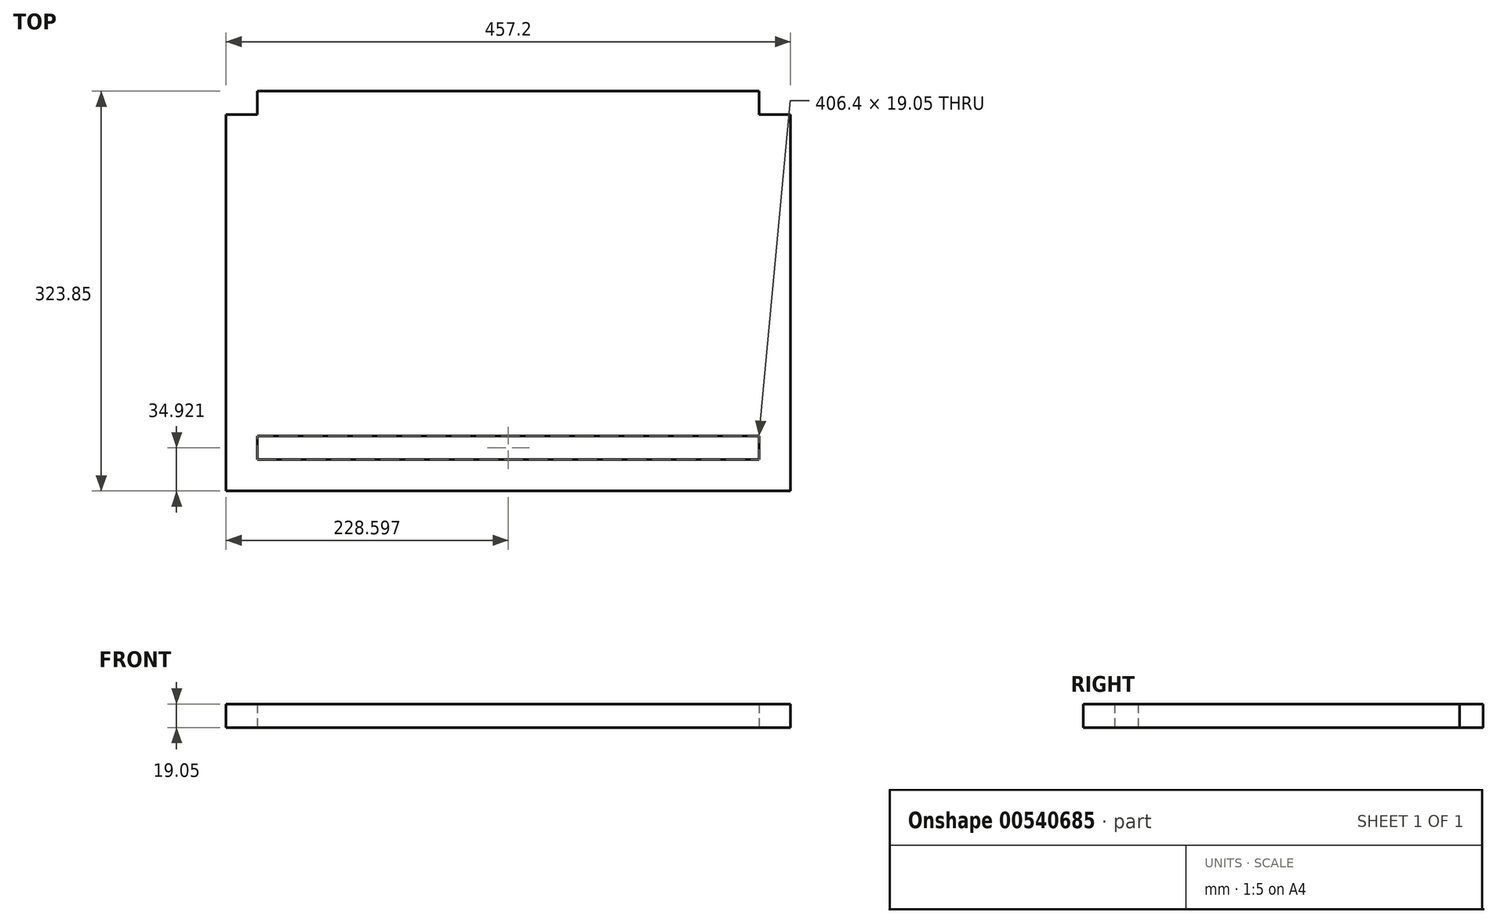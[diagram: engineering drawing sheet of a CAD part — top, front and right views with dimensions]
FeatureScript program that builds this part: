
annotation { "Feature Type Name" : "Feature", "Feature Type Description" : "" }
export const myFeature = defineFeature(function(context is Context, id is Id, definition is map)
    precondition{}
    {
        {
            var Q0;
            Q0=qCreatedBy(makeId("Top.planeOp"),FACE);
            var sketch = newSketch(context, id + "F0", { "sketchPlane" : qUnion([Q0])});
            skLineSegment(sketch, "E0.bottom", {"start": v(-236.05, -85.37) * mm, "end": v(-210.65, -85.37) * mm});
            skLineSegment(sketch, "E0.top", {"start": v(-236.05, -390.17) * mm, "end": v(221.15, -390.17) * mm});
            skLineSegment(sketch, "E0.left", {"start": v(-236.05, -85.37) * mm, "end": v(-236.05, -390.17) * mm});
            skLineSegment(sketch, "E0.right", {"start": v(221.15, -85.37) * mm, "end": v(221.15, -390.17) * mm});
            skLineSegment(sketch, "E1", {"start": v(-210.65, -85.37) * mm, "end": v(-210.65, -66.32) * mm});
            skLineSegment(sketch, "E2", {"start": v(-210.65, -66.32) * mm, "end": v(195.75, -66.32) * mm});
            skLineSegment(sketch, "E3", {"start": v(195.75, -66.32) * mm, "end": v(195.75, -85.37) * mm});
            skLineSegment(sketch, "E4.trimOffspring", {"start": v(195.75, -85.37) * mm, "end": v(221.15, -85.37) * mm});
            skLineSegment(sketch, "E5.0", {"start": v(-210.65, -364.77) * mm, "end": v(195.75, -364.77) * mm});
            skLineSegment(sketch, "E6.0", {"start": v(-210.65, -345.72) * mm, "end": v(-210.65, -364.77) * mm});
            skLineSegment(sketch, "E7.0", {"start": v(195.75, -345.72) * mm, "end": v(195.75, -364.77) * mm});
            skLineSegment(sketch, "E8.0", {"start": v(-210.65, -345.72) * mm, "end": v(195.75, -345.72) * mm});
            skSolve(sketch);
        }
        {
            var Q0;
            Q0 = qSketchRegion(id + "F0", true);
            extrude(context, id + "F1", {"entities" : qUnion([Q0]), "depth" : 19.05 * mm, "offsetDistance" : 25.4 * mm});
        }
    });
